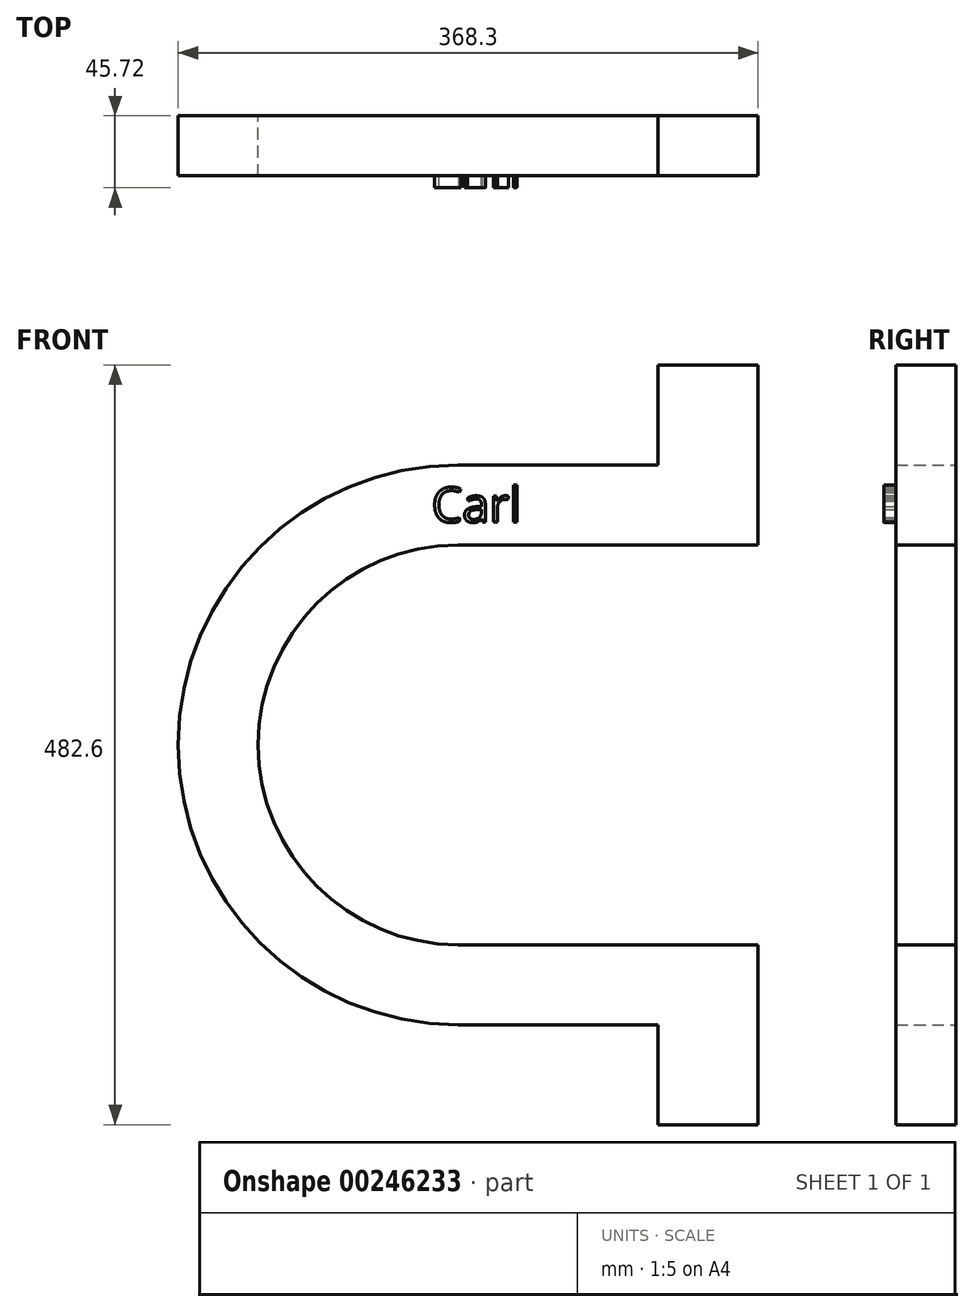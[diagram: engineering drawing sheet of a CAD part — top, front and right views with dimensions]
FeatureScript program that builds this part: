
annotation { "Feature Type Name" : "Feature", "Feature Type Description" : "" }
export const myFeature = defineFeature(function(context is Context, id is Id, definition is map)
    precondition{}
    {
        {
            var Q0;
            Q0=qCreatedBy(makeId("Front.planeOp"),FACE);
            var sketch = newSketch(context, id + "F0", { "sketchPlane" : qUnion([Q0])});
            skLineSegment(sketch, "E0.bottom", {"start": v(0, 177.8) * mm, "end": v(127, 177.8) * mm});
            skLineSegment(sketch, "E0.top", {"start": v(0, -177.8) * mm, "end": v(127, -177.8) * mm});
            skLineSegment(sketch, "E0.right", {"start": v(190.5, 177.8) * mm, "end": v(190.5, 127) * mm});
            skPoint(sketch, "E0.middle", {"position": v(0, 0) * mm});
            skArc(sketch, "E1", {"start": v(0, 127) * mm, "mid": v(-127, 0) * mm, "end": v(0, -127) * mm});
            skLineSegment(sketch, "E2", {"start": v(0, 127) * mm, "end": v(190.5, 127) * mm});
            skLineSegment(sketch, "E3", {"start": v(0, -127) * mm, "end": v(190.5, -127) * mm});
            skLineSegment(sketch, "E4.bottom", {"start": v(190.5, -127) * mm, "end": v(127, -127) * mm});
            skLineSegment(sketch, "E4.left", {"start": v(190.5, -127) * mm, "end": v(190.5, -177.8) * mm});
            skLineSegment(sketch, "E5.bottom", {"start": v(190.5, 127) * mm, "end": v(127, 127) * mm});
            skLineSegment(sketch, "E5.left", {"start": v(190.5, 127) * mm, "end": v(190.5, 177.8) * mm});
            skPoint(sketch, "E6.orphan", {"position": v(-190.5, 177.8) * mm});
            skPoint(sketch, "E7.orphan", {"position": v(-190.5, -177.8) * mm});
            skLineSegment(sketch, "E8", {"start": v(-191.74, 177.8) * mm, "end": v(-190.5, 177.8) * mm});
            skArc(sketch, "E9", {"start": v(-177.8, 0) * mm, "mid": v(-125.72, -125.72) * mm, "end": v(0, -177.8) * mm});
            skPoint(sketch, "E9.startSnap0", {"position": v(-127, 0) * mm});
            skArc(sketch, "E10", {"start": v(-177.8, 0) * mm, "mid": v(-125.72, 125.72) * mm, "end": v(0, 177.8) * mm});
            skPoint(sketch, "E11.orphan", {"position": v(190.5, -190.5) * mm});
            skPoint(sketch, "E12.orphan", {"position": v(190.5, 190.5) * mm});
            skLineSegment(sketch, "E13.left", {"start": v(127, 177.8) * mm, "end": v(127, 177.8) * mm});
            skLineSegment(sketch, "E13.right", {"start": v(190.5, 177.8) * mm, "end": v(190.5, 177.8) * mm});
            skLineSegment(sketch, "E14.top", {"start": v(127, 241.3) * mm, "end": v(190.5, 241.3) * mm});
            skLineSegment(sketch, "E14.left", {"start": v(127, 177.8) * mm, "end": v(127, 241.3) * mm});
            skLineSegment(sketch, "E14.right", {"start": v(190.5, 177.8) * mm, "end": v(190.5, 241.3) * mm});
            skLineSegment(sketch, "E15.bottom", {"start": v(127, -241.3) * mm, "end": v(190.5, -241.3) * mm});
            skLineSegment(sketch, "E15.left", {"start": v(127, -241.3) * mm, "end": v(127, -177.8) * mm});
            skLineSegment(sketch, "E15.right", {"start": v(190.5, -241.3) * mm, "end": v(190.5, -177.8) * mm});
            skSolve(sketch);
        }
        {
            var Q0;
            Q0=makeQuery(id+"F0.imprint","IMPRINT",FACE,{"disambiguationData":[TD([[makeQuery(id+"F0.imprint","IMPRINT",EDGE,{"derivedFrom":sQuery(id+"F0.wireOp",EDGE,"E0.bottom")}),-1.0]])]});
            extrude(context, id + "F1", {"entities" : qUnion([Q0]), "depth" : 38.1 * mm});
        }
        {
            var Q0;
            Q0=qCreatedBy(makeId("Front.planeOp"),FACE);
            var sketch = newSketch(context, id + "F2", { "sketchPlane" : qUnion([Q0])});
            skText(sketch, "E16", { "text": "Carl\n", "fontName": "OpenSans-Regular.ttf"});
            const initialGuessF2  = {"E16": [-0.01681, 0.1414, 1, 0, 0.0222]};
            skSetInitialGuess(sketch, initialGuessF2);
            skSolve(sketch);
        }
        {
            var Q0;
            Q0 = qSketchRegion(id + "F2", true);
            extrude(context, id + "F3", {"entities" : qUnion([Q0]), "operationType" : NewBodyOperationType.ADD, "depth" : 45.72 * mm});
        }
    });
